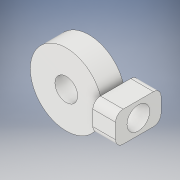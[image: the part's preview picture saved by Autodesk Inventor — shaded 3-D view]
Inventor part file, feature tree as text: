
AUTODESK INVENTOR PART (.ipt)
format: ipt  version: 2017 SP1 (Build 210196100, 196)  size: 145,408 bytes
history: native  units: in
note: dims shown in document units (in); Inventor stores cm internally (conversion verified against a paired STEP export)
features: extrude x4, sketch x4, fillet x1
ambient origin geometry x8: Origin, YZ Plane, XZ Plane, XY Plane, X Axis, Y Axis, Z Axis, Center Point
bodies: Solid1 (feature_tree)
feature tree (9):
  extrude  "Extrusion1"  Depth=0.1181in
  extrude  "Extrusion2"  Depth=0.1181in
  extrude  "Extrusion3"  Depth=0.1181in TaperAngle=0.0deg
  fillet  "Fillet1"  Radius=0.2362in
  extrude  "Extrusion4"  Depth=0.1181in TaperAngle=0.0deg
  sketch  "Sketch1"  dims[d0=0.1181in d1=0.374in]
  sketch  "Sketch2"  dims[d2=0.1181in d3=0.0in d4=0.1181in]
  sketch  "Sketch4"  dims[d5=0.0197in d6=0.1181in d7=0.0in d9=0.2362in]
  sketch  "Sketch6"  dims[d10=0.1575in d11=0.1181in d12=0.0in d13=0.0394in d14=0.1181in d15=0.1181in d16=0.0in]
